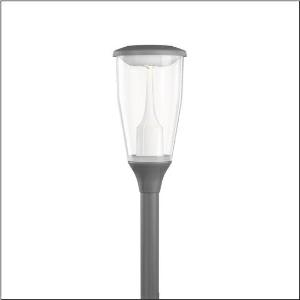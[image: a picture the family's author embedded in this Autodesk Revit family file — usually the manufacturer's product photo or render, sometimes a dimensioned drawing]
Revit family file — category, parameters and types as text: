
# Revit family: dl_11_iq___p1_0a_5xa5565bf14hp00022_ddba
name_source: partatom
category: Lighting Fixtures
units: mm (PartAtom-declared; Revit-internal decimal feet)

## family parameters
Cut with Voids When Loaded = No
Host = Face
Light Source = No
Part Type = Normal
Room Calculation Point = No
Round Connector Dimension = Use Diameter
Shared = No

## types (1)
- --- (1 x LED, 3950 lm, 33.6 W, 2200K)
    Apparent Load = 34 VA
    CIE Flux Codes = 23 60 93 95 100
    Color Rendering = 70
    Color Temperature = 2200K
    Default Elevation = 1800 mm
    Description = DL 11 iQ, mast luminaire, Module 540 iQ-SR, primary light control with 3 zone facetted reflector, of plastic, silver coated, highly specular, structured, primary optical cover: cover, of PMMA, transparent, light distribution: P1.0a, light emission: direct distribution, primary light characteristic: asymmetric, installation type: post-top, LED, High Power LED, light colour: 722, colour temperature: 2200K, control: Street-Remote, Auto-Match, Temp-Guard, Lumen-Switch, Night-Set, Smart-Wire, Light-Fading, Desk-Remote (wireless, voltage-free reading and setting of iQ features in the workshop via application-optimized NFC function/RFID function), optimised constant luminous flux control (CLO 2.0), mains connection: 220..240V, AC, 50/60Hz, connection cable pre-assembled, cable length: 5,5m, start of lifetime: 34W, end of service life: 36W, luminaire housing, upper part, of diecast aluminium, coated, Siteco® metallic grey (DB 702S), spigot size: 60mm (post-top), post-top mast mounting element, of diecast aluminium, coated, Siteco® metallic grey (DB 702S), Module 540 iQ-SR, traffic white (RAL 9016), equipment: Power, protection rating (complete): IP66, insulation class (complete): insulation class II (safety insulation), certification: CE, ENEC, ENEC+, VDE, packaging unit: 1 piece

Light Distribution: P1.0a
    Height = 665 mm
    Lamp = 1 x LED
    Lamp Light Flux = 3950 lm
    Lamp Power = 33.6 W
    Lamp count = 1
    Length = 334 mm
    Luminous efficacy = 118 lm/W
    Manufacturer = Siteco
    ModVariant = No
    Model = 5XA5565BF14HP00022
    Number of Poles = 1
    OnlyDefault = Yes
    Power Factor = 1
    Product Name = DL 11 iQ | P1.0a
    Product group = mast luminaire | pylon top
    ProductGroupID = 6100
    Protection Class = Protection class II
    Protection Degree = IP 66
    RLX_Detail_Level = 1
    RLX_Emergency_Light_Flux = 0 lm
    RLX_Emergency_Type = 0
    RLX_Emergency_Type_DB = No
    RlxData = <blob elided: 104101 chars, md5=78d529b7>
    Socket = socket
    Standby Power = 0 W
    System Light Flux = 3950 lm
    System Power = 34 W
    Type Comments = factory setting: luminous flux: 100 % | dim-lin: 254 | 695 mA
    Type Image = l_1258354.jpg
    URL = http://relux.com
    VarID = @adj_022011
    Voltage = 0 V
    Weight = 0.00 kg
    Width = 0 mm  [stored 0 ft]

note: [stored X ft] marks values corroborated as IEEE doubles in the binary element streams (Revit-internal decimal feet)

## geometry (parser evidence)
native form markers: Blend x4, Sweep x11
no freeform markers — native parametric forms only
